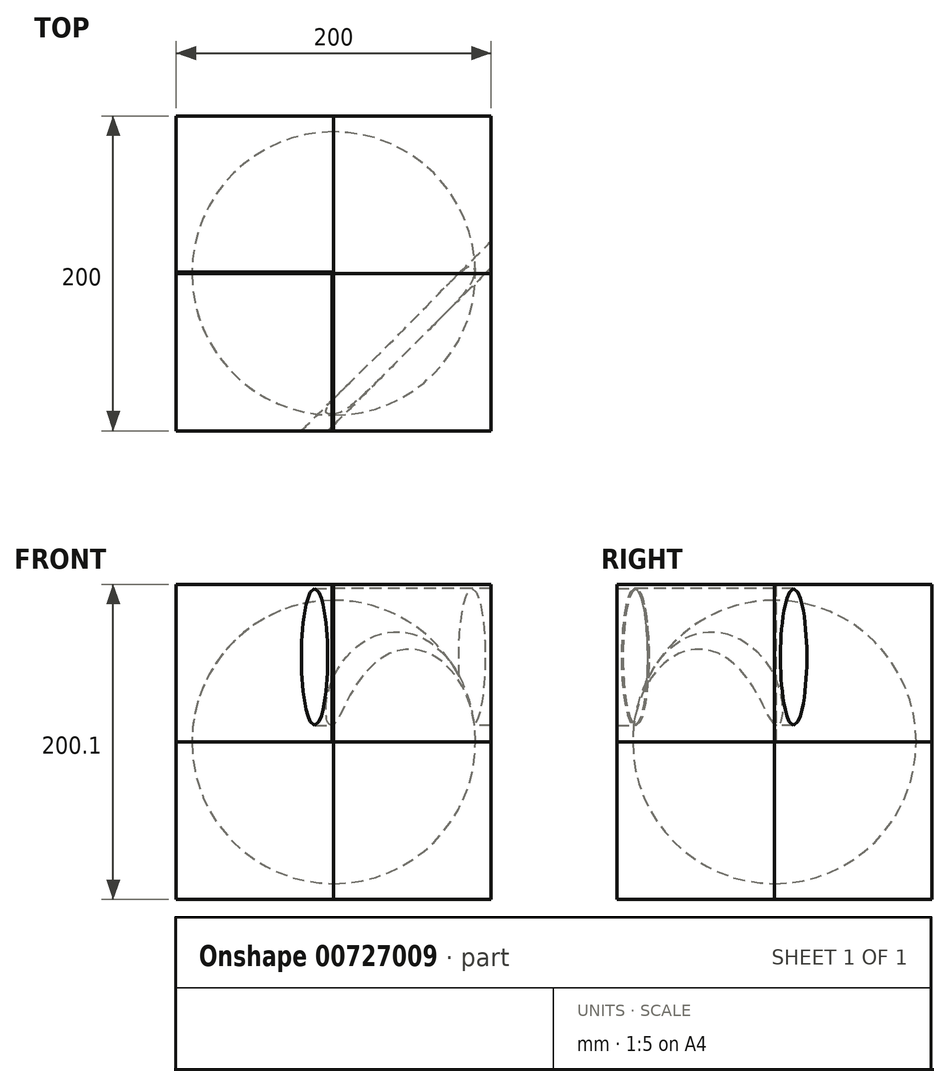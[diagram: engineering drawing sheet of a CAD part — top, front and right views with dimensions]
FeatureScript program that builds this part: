
annotation { "Feature Type Name" : "Feature", "Feature Type Description" : "" }
export const myFeature = defineFeature(function(context is Context, id is Id, definition is map)
    precondition{}
    {
        {
            var Q0;
            Q0=qCreatedBy(makeId("Top.planeOp"),FACE);
            var sketch = newSketch(context, id + "F0", { "sketchPlane" : qUnion([Q0])});
            skLineSegment(sketch, "E0.bottom", {"start": v(0, 0) * mm, "end": v(-100, 0) * mm});
            skLineSegment(sketch, "E0.top", {"start": v(0, 100) * mm, "end": v(-100, 100) * mm});
            skLineSegment(sketch, "E0.left", {"start": v(0, 0) * mm, "end": v(0, 100) * mm});
            skLineSegment(sketch, "E0.right", {"start": v(-100, 0) * mm, "end": v(-100, 100) * mm});
            skSolve(sketch);
        }
        {
            var Q0;
            Q0=makeQuery(id+"F0.imprint","IMPRINT",FACE,{"disambiguationData":[TD([[makeQuery(id+"F0.imprint","IMPRINT",EDGE,{"derivedFrom":sQuery(id+"F0.wireOp",EDGE,"E0.bottom")}),-1.0]])]});
            extrude(context, id + "F1", {"entities" : qUnion([Q0]), "depth" : 100 * mm, "offsetDistance" : 25 * mm});
        }
        {
            var Q0;
            Q0=qCreatedBy(makeId("Top.planeOp"),FACE);
            var sketch = newSketch(context, id + "F2", { "sketchPlane" : qUnion([Q0])});
            skLineSegment(sketch, "E1.bottom", {"start": v(0, 0) * mm, "end": v(100, 0) * mm});
            skLineSegment(sketch, "E1.top", {"start": v(0, 100) * mm, "end": v(100, 100) * mm});
            skLineSegment(sketch, "E1.left", {"start": v(0, 0) * mm, "end": v(0, 100) * mm});
            skLineSegment(sketch, "E1.right", {"start": v(100, 0) * mm, "end": v(100, 100) * mm});
            skSolve(sketch);
        }
        {
            var Q0;
            Q0=makeQuery(id+"F2.imprint","IMPRINT",FACE,{"disambiguationData":[TD([[makeQuery(id+"F2.imprint","IMPRINT",EDGE,{"derivedFrom":sQuery(id+"F2.wireOp",EDGE,"E1.bottom")}),1.0]])]});
            var Q1;
            Q1 = qSketchRegion(id + "F2", true);
            extrude(context, id + "F3", {"entities" : qUnion([Q0, Q1]), "depth" : 100 * mm, "offsetDistance" : 25 * mm});
        }
        {
            var Q0;
            Q0=qCreatedBy(makeId("Top.planeOp"),FACE);
            var sketch = newSketch(context, id + "F4", { "sketchPlane" : qUnion([Q0])});
            skLineSegment(sketch, "E2.bottom", {"start": v(0, 0) * mm, "end": v(-100, 0) * mm});
            skLineSegment(sketch, "E2.top", {"start": v(0, -100) * mm, "end": v(-100, -100) * mm});
            skLineSegment(sketch, "E2.left", {"start": v(0, 0) * mm, "end": v(0, -100) * mm});
            skLineSegment(sketch, "E2.right", {"start": v(-100, 0) * mm, "end": v(-100, -100) * mm});
            skSolve(sketch);
        }
        {
            var Q0;
            Q0=makeQuery(id+"F4.imprint","IMPRINT",FACE,{"disambiguationData":[TD([[makeQuery(id+"F4.imprint","IMPRINT",EDGE,{"derivedFrom":sQuery(id+"F4.wireOp",EDGE,"E2.bottom")}),1.0]])]});
            extrude(context, id + "F5", {"entities" : qUnion([Q0]), "depth" : 100 * mm, "offsetDistance" : 25 * mm});
        }
        {
            var Q0;
            Q0=qCreatedBy(makeId("Top.planeOp"),FACE);
            var sketch = newSketch(context, id + "F6", { "sketchPlane" : qUnion([Q0])});
            skLineSegment(sketch, "E3.bottom", {"start": v(0, 0) * mm, "end": v(100, 0) * mm});
            skLineSegment(sketch, "E3.top", {"start": v(0, -100) * mm, "end": v(100, -100) * mm});
            skLineSegment(sketch, "E3.left", {"start": v(0, 0) * mm, "end": v(0, -100) * mm});
            skLineSegment(sketch, "E3.right", {"start": v(100, 0) * mm, "end": v(100, -100) * mm});
            skSolve(sketch);
        }
        {
            var Q0;
            Q0=makeQuery(id+"F6.imprint","IMPRINT",FACE,{"disambiguationData":[TD([[makeQuery(id+"F6.imprint","IMPRINT",EDGE,{"derivedFrom":sQuery(id+"F6.wireOp",EDGE,"E3.bottom")}),-1.0]])]});
            extrude(context, id + "F7", {"entities" : qUnion([Q0]), "depth" : 100 * mm, "offsetDistance" : 25 * mm});
        }
        {
            var Q0;
            Q0=qCreatedBy(makeId("Top.planeOp"),FACE);
            var sketch = newSketch(context, id + "F8", { "sketchPlane" : qUnion([Q0])});
            skLineSegment(sketch, "E4.bottom", {"start": v(0, 0) * mm, "end": v(100, 0) * mm});
            skLineSegment(sketch, "E4.top", {"start": v(0, -100) * mm, "end": v(100, -100) * mm});
            skLineSegment(sketch, "E4.left", {"start": v(0, 0) * mm, "end": v(0, -100) * mm});
            skLineSegment(sketch, "E4.right", {"start": v(100, 0) * mm, "end": v(100, -100) * mm});
            skSolve(sketch);
        }
        {
            var Q0;
            Q0=makeQuery(id+"F8.imprint","IMPRINT",FACE,{"disambiguationData":[TD([[makeQuery(id+"F8.imprint","IMPRINT",EDGE,{"derivedFrom":sQuery(id+"F8.wireOp",EDGE,"E4.bottom")}),-1.0]])]});
            extrude(context, id + "F9", {"entities" : qUnion([Q0]), "oppositeDirection" : true, "depth" : 100 * mm, "offsetDistance" : 25 * mm});
        }
        {
            var Q0;
            Q0=qCreatedBy(makeId("Top.planeOp"),FACE);
            var sketch = newSketch(context, id + "F10", { "sketchPlane" : qUnion([Q0])});
            skLineSegment(sketch, "E5.bottom", {"start": v(0, 0) * mm, "end": v(-100, 0) * mm});
            skLineSegment(sketch, "E5.top", {"start": v(0, -100) * mm, "end": v(-100, -100) * mm});
            skLineSegment(sketch, "E5.left", {"start": v(0, 0) * mm, "end": v(0, -100) * mm});
            skLineSegment(sketch, "E5.right", {"start": v(-100, 0) * mm, "end": v(-100, -100) * mm});
            skSolve(sketch);
        }
        {
            var Q0;
            Q0=makeQuery(id+"F10.imprint","IMPRINT",FACE,{"disambiguationData":[TD([[makeQuery(id+"F10.imprint","IMPRINT",EDGE,{"derivedFrom":sQuery(id+"F10.wireOp",EDGE,"E5.bottom")}),1.0]])]});
            extrude(context, id + "F11", {"entities" : qUnion([Q0]), "oppositeDirection" : true, "depth" : 100 * mm, "offsetDistance" : 25 * mm});
        }
        {
            var Q0;
            Q0=qCreatedBy(makeId("Top.planeOp"),FACE);
            var sketch = newSketch(context, id + "F12", { "sketchPlane" : qUnion([Q0])});
            skLineSegment(sketch, "E6.bottom", {"start": v(0, 0) * mm, "end": v(100, 0) * mm});
            skLineSegment(sketch, "E6.top", {"start": v(0, 100) * mm, "end": v(100, 100) * mm});
            skLineSegment(sketch, "E6.left", {"start": v(0, 0) * mm, "end": v(0, 100) * mm});
            skLineSegment(sketch, "E6.right", {"start": v(100, 0) * mm, "end": v(100, 100) * mm});
            skSolve(sketch);
        }
        {
            var Q0;
            Q0=makeQuery(id+"F12.imprint","IMPRINT",FACE,{"disambiguationData":[TD([[makeQuery(id+"F12.imprint","IMPRINT",EDGE,{"derivedFrom":sQuery(id+"F12.wireOp",EDGE,"E6.bottom")}),1.0]])]});
            extrude(context, id + "F13", {"entities" : qUnion([Q0]), "oppositeDirection" : true, "depth" : 100 * mm, "offsetDistance" : 25 * mm});
        }
        {
            var Q0;
            Q0=qCreatedBy(makeId("Top.planeOp"),FACE);
            var sketch = newSketch(context, id + "F14", { "sketchPlane" : qUnion([Q0])});
            skLineSegment(sketch, "E7.bottom", {"start": v(0, 0) * mm, "end": v(-100, 0) * mm});
            skLineSegment(sketch, "E7.top", {"start": v(0, 100) * mm, "end": v(-100, 100) * mm});
            skLineSegment(sketch, "E7.left", {"start": v(0, 0) * mm, "end": v(0, 100) * mm});
            skLineSegment(sketch, "E7.right", {"start": v(-100, 0) * mm, "end": v(-100, 100) * mm});
            skSolve(sketch);
        }
        {
            var Q0;
            Q0=makeQuery(id+"F14.imprint","IMPRINT",FACE,{"disambiguationData":[TD([[makeQuery(id+"F14.imprint","IMPRINT",EDGE,{"derivedFrom":sQuery(id+"F14.wireOp",EDGE,"E7.bottom")}),-1.0]])]});
            extrude(context, id + "F15", {"entities" : qUnion([Q0]), "oppositeDirection" : true, "depth" : 100 * mm, "offsetDistance" : 25 * mm});
        }
        {
            var Q0;
            Q0=qCreatedBy(makeId("Front.planeOp"),FACE);
            var sketch = newSketch(context, id + "F16", { "sketchPlane" : qUnion([Q0])});
            skArc(sketch, "E8", {"start": v(0, -90) * mm, "mid": v(90, 0) * mm, "end": v(0, 90) * mm});
            skLineSegment(sketch, "E9", {"start": v(0, 90) * mm, "end": v(0, -90) * mm});
            skLineSegment(sketch, "E10", {"start": v(0, 156.12) * mm, "end": v(0, -217.45) * mm});
            skSolve(sketch);
        }
        {
            var Q0;
            {var subQ0=sQuery(id+"F16.wireOp",EDGE,"E8");Q0=makeQuery(id+"F16.imprint","IMPRINT",FACE,{"disambiguationData":[TD([[makeQuery(id+"F16.imprint","IMPRINT",EDGE,{"derivedFrom":subQ0}),1.0]])]});}
            var Q1;
            Q1=sQuery(id+"F16.wireOp",EDGE,"E10");
            revolve(context, id + "F17", {"operationType" : NewBodyOperationType.REMOVE, "surfaceOperationType" : NewSurfaceOperationType.NEW, "entities" : qUnion([Q0]), "axis" : qUnion([Q1]), "revolveType" : RevolveType.FULL});
        }
        {
            var Q0;
            Q0=makeQuery(id+"F5.opExtrude","SWEPT_FACE",FACE,{"disambiguationData":[OSD([sQuery(id+"F4.wireOp",EDGE,"E2.left")])]});
            var sketch = newSketch(context, id + "F18", { "sketchPlane" : qUnion([Q0])});
            skLineSegment(sketch, "E11.bottom", {"start": v(-100, 100) * mm, "end": v(0, 100) * mm});
            skLineSegment(sketch, "E11.top", {"start": v(-100, 0) * mm, "end": v(0, 0) * mm});
            skLineSegment(sketch, "E11.left", {"start": v(-100, 100) * mm, "end": v(-100, 0) * mm});
            skLineSegment(sketch, "E11.right", {"start": v(0, 100) * mm, "end": v(0, 0) * mm});
            skSolve(sketch);
        }
        {
            var Q0;
            Q0 = qSketchRegion(id + "F18", true);
            extrude(context, id + "F19", {"entities" : qUnion([Q0]), "operationType" : NewBodyOperationType.REMOVE, "oppositeDirection" : true, "depth" : 1 * mm, "offsetDistance" : 25 * mm});
        }
        {
            var Q0;
            Q0=makeQuery(id+"F19.boolean.opBoolean","COPY",FACE,{"derivedFrom":makeQuery(id+"F19.opExtrude","CAP_FACE",FACE,{"disambiguationData":[OSD([sQuery(id+"F18.wireOp",EDGE,"E11.bottom"),sQuery(id+"F18.wireOp",EDGE,"E11.top"),sQuery(id+"F18.wireOp",EDGE,"E11.left"),sQuery(id+"F18.wireOp",EDGE,"E11.right")])],"isStart":false})});
            var sketch = newSketch(context, id + "F20", { "sketchPlane" : qUnion([Q0])});
            skLineSegment(sketch, "E12.bottom", {"start": v(-100, 100) * mm, "end": v(0, 100) * mm});
            skLineSegment(sketch, "E12.top", {"start": v(-100, 0) * mm, "end": v(0, 0) * mm});
            skLineSegment(sketch, "E12.left", {"start": v(-100, 100) * mm, "end": v(-100, 0) * mm});
            skLineSegment(sketch, "E12.right", {"start": v(0, 100) * mm, "end": v(0, 0) * mm});
            skSolve(sketch);
        }
        {
            var Q0;
            Q0 = qSketchRegion(id + "F20", true);
            extrude(context, id + "F21", {"entities" : qUnion([Q0]), "depth" : 1 * mm, "offsetDistance" : 25 * mm});
        }
        {
            var Q0;
            Q0=makeQuery(id+"F5.opExtrude","SWEPT_FACE",FACE,{"disambiguationData":[OSD([sQuery(id+"F4.wireOp",EDGE,"E2.bottom")])]});
            var sketch = newSketch(context, id + "F22", { "sketchPlane" : qUnion([Q0])});
            skLineSegment(sketch, "E13.bottom", {"start": v(100, 100) * mm, "end": v(0, 100) * mm});
            skLineSegment(sketch, "E13.top", {"start": v(100, 0) * mm, "end": v(0, 0) * mm});
            skLineSegment(sketch, "E13.left", {"start": v(100, 100) * mm, "end": v(100, 0) * mm});
            skLineSegment(sketch, "E13.right", {"start": v(0, 100) * mm, "end": v(0, 0) * mm});
            skSolve(sketch);
        }
        {
            var Q0;
            {var subQ1=sQuery(id+"F22.wireOp",EDGE,"E13.left");Q0=makeQuery(id+"F22.imprint","IMPRINT",FACE,{"disambiguationData":[TD([[makeQuery(id+"F22.imprint","IMPRINT",EDGE,{"derivedFrom":subQ1}),-1.0]])]});}
            var sketch = newSketch(context, id + "F23", { "sketchPlane" : qUnion([Q0])});
            skLineSegment(sketch, "E14.bottom", {"start": v(0, 100.1) * mm, "end": v(99.95, 100.1) * mm});
            skLineSegment(sketch, "E14.top", {"start": v(0, 0) * mm, "end": v(99.95, 0) * mm});
            skLineSegment(sketch, "E14.left", {"start": v(0, 100.1) * mm, "end": v(0, 0) * mm});
            skLineSegment(sketch, "E14.right", {"start": v(99.95, 100.1) * mm, "end": v(99.95, 0) * mm});
            skSolve(sketch);
        }
        {
            var Q0;
            Q0 = qSketchRegion(id + "F23", true);
            extrude(context, id + "F24", {"entities" : qUnion([Q0]), "depth" : 1 * mm, "offsetDistance" : 25 * mm});
        }
        {
            var Q0;
            Q0=makeQuery(id+"F24.opExtrude","CAP_EDGE",EDGE,{"disambiguationData":[OSD([sQuery(id+"F23.wireOp",EDGE,"E14.left")])],"isStart":false});
            fillet(context, id + "F25", {"entities" : qUnion([Q0]), "radius" : 0.5 * mm, "tangentPropagation" : true, "allowEdgeOverflow" : false});
        }
        {
            var Q0;
            Q0=makeQuery(id+"F21.opExtrude","CAP_EDGE",EDGE,{"disambiguationData":[OSD([sQuery(id+"F20.wireOp",EDGE,"E12.right")])],"isStart":false});
            fillet(context, id + "F26", {"entities" : qUnion([Q0]), "radius" : 0.5 * mm, "tangentPropagation" : true, "allowEdgeOverflow" : false});
        }
        {
            var Q0;
            Q0=makeQuery(id+"F21.opExtrude","CAP_EDGE",EDGE,{"disambiguationData":[OSD([sQuery(id+"F20.wireOp",EDGE,"E12.left")])],"isStart":false});
            cPlane(context, id + "F27", {"entities" : qUnion([Q0]), "cplaneType" : CPlaneType.LINE_ANGLE, "offset" : 25 * mm, "angle" : 45 * degree, "oppositeDirection" : true, "width" : 150 * mm, "height" : 150 * mm});
        }
        {
            var Q0;
            Q0=qCreatedBy(id+"F27.planeOp",FACE);
            var sketch = newSketch(context, id + "F28", { "sketchPlane" : qUnion([Q0])});
            skEllipse(sketch, "E15", {"center": v(62.13, 53.96) * mm, "majorRadius": 43.45 * mm, "minorRadius": 5.91 * mm, "majorAxis": v(0, 1)});
            skSolve(sketch);
        }
        {
            var Q0;
            Q0=makeQuery(id+"F24.opExtrude","CAP_EDGE",EDGE,{"disambiguationData":[OSD([sQuery(id+"F23.wireOp",EDGE,"E14.top")])],"isStart":false});
            var Q1;
            Q1=makeQuery(id+"F21.opExtrude","CAP_EDGE",EDGE,{"disambiguationData":[OSD([sQuery(id+"F20.wireOp",EDGE,"E12.top")])],"isStart":false});
            var Q2;
            Q2=makeQuery(id+"F5.opExtrude","CAP_EDGE",EDGE,{"disambiguationData":[OSD([sQuery(id+"F4.wireOp",EDGE,"E2.right")])],"isStart":true});
            var Q3;
            Q3=makeQuery(id+"F5.opExtrude","CAP_EDGE",EDGE,{"disambiguationData":[OSD([sQuery(id+"F4.wireOp",EDGE,"E2.top")])],"isStart":true});
            fillet(context, id + "F29", {"entities" : qUnion([Q0, Q1, Q2, Q3]), "radius" : 0.5 * mm, "tangentPropagation" : true, "allowEdgeOverflow" : false});
        }
        {
            var Q0;
            Q0 = qSketchRegion(id + "F28", true);
            extrude(context, id + "F30", {"entities" : qUnion([Q0]), "operationType" : NewBodyOperationType.REMOVE, "endBound" : BoundingType.THROUGH_ALL, "depth" : 100 * mm, "offsetDistance" : 25 * mm});
        }
        {
            var Q0;
            Q0 = qSketchRegion(id + "F28", true);
            extrude(context, id + "F31", {"entities" : qUnion([Q0]), "operationType" : NewBodyOperationType.REMOVE, "endBound" : BoundingType.THROUGH_ALL, "oppositeDirection" : true, "depth" : 25 * mm, "offsetDistance" : 25 * mm});
        }
    });
